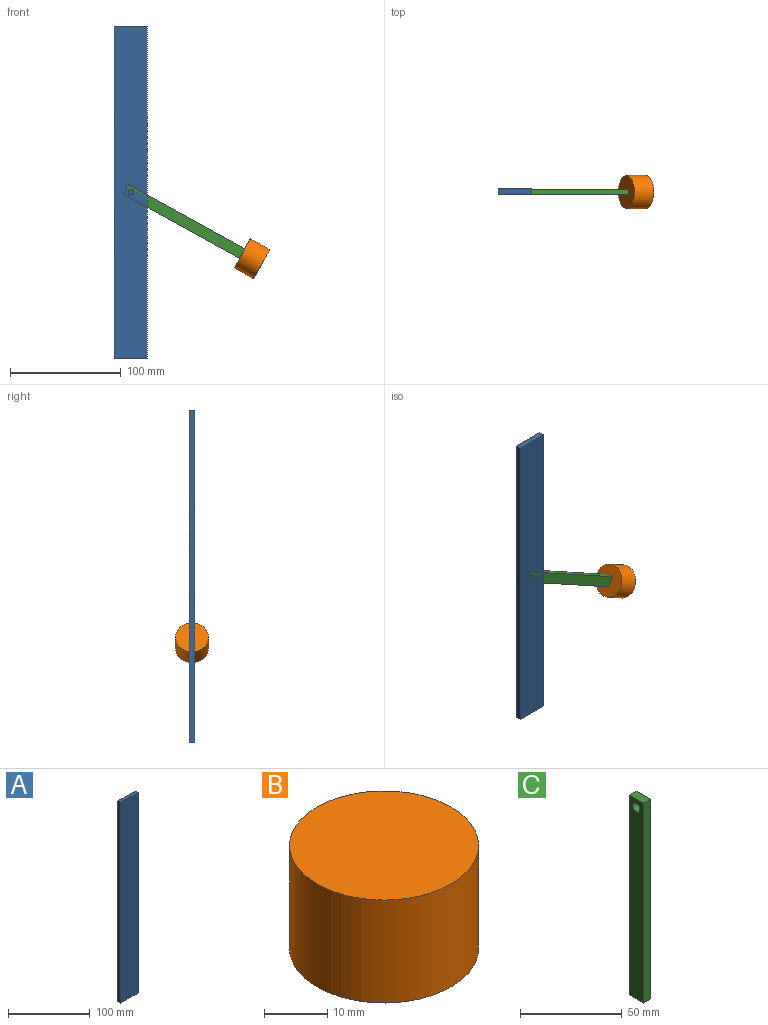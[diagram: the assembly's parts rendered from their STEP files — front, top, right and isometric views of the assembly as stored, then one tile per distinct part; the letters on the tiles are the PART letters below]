
ASSEMBLY  parts=3 mates=3
PART A: 6 faces, bbox 30x5x300 mm
  f0: plane 30x5mm, normal (0,0,1), area 150mm2, adj f1,f3,f4,f5
  f1: plane 300x5mm, normal (-1,0,0), area 1500mm2, adj f0,f2,f4,f5
  f2: plane 30x5mm, normal (0,0,-1), area 150mm2, adj f1,f3,f4,f5
  f3: plane 300x5mm, normal (1,0,0), area 1500mm2, adj f0,f2,f4,f5
  f4: plane 300x30mm, normal (0,-1,0), area 9000mm2, adj f0,f1,f2,f3
  f5: plane 300x30mm, normal (0,1,0), area 9000mm2, adj f0,f1,f2,f3
PART B: 3 faces, bbox 30x30x20 mm
  f0: cylinder r=15mm len=30mm, axis (0,0,-1), area 1885mm2, adj f1,f2
  f1: plane 30x30mm, normal (0,0,1), area 706.9mm2, adj f0
  f2: plane 30x30mm, normal (0,0,-1), area 706.9mm2, adj f0
PART C: 7 faces, bbox 5x10x120 mm
  f0: plane 10x5mm, normal (0,0,1), area 50mm2, adj f1,f3,f4,f5
  f1: plane 120x5mm, normal (0,-1,0), area 600mm2, adj f0,f2,f4,f5
  f2: plane 10x5mm, normal (0,0,-1), area 50mm2, adj f1,f3,f4,f5
  f3: plane 120x5mm, normal (0,1,0), area 600mm2, adj f0,f2,f4,f5
  f4: plane 120x10mm, normal (1,0,0), area 1180.4mm2, adj f0,f1,f2,f3,f6
  f5: plane 120x10mm, normal (-1,0,0), area 1180.4mm2, adj f0,f1,f2,f3,f6
  f6: cylinder r=2.5mm len=5mm, axis (-1,0,0), area 78.5mm2, adj f4,f5
PLACE A at identity fixed
PLACE B rot(axis=(0,-1,0),61.1deg) t=(91.6,-2.5,-24.33)mm
PLACE C rot(axis=(0.45,-0.45,-0.77),105deg) t=(23.32,0,25.64)mm
MATE pin_slot C.f6 <-> A.f4  axis (0,-1,0) through (-46.69,-5,4.42)mm
MATE fastened C.f2 <-> B.f0  axis (0.88,0,-0.48) through (54.02,-2.5,-51.09)mm
MATE pin_slot A.f4 <-> C.f6  axis (0,-1,0) through (-46.69,-5,4.42)mm
